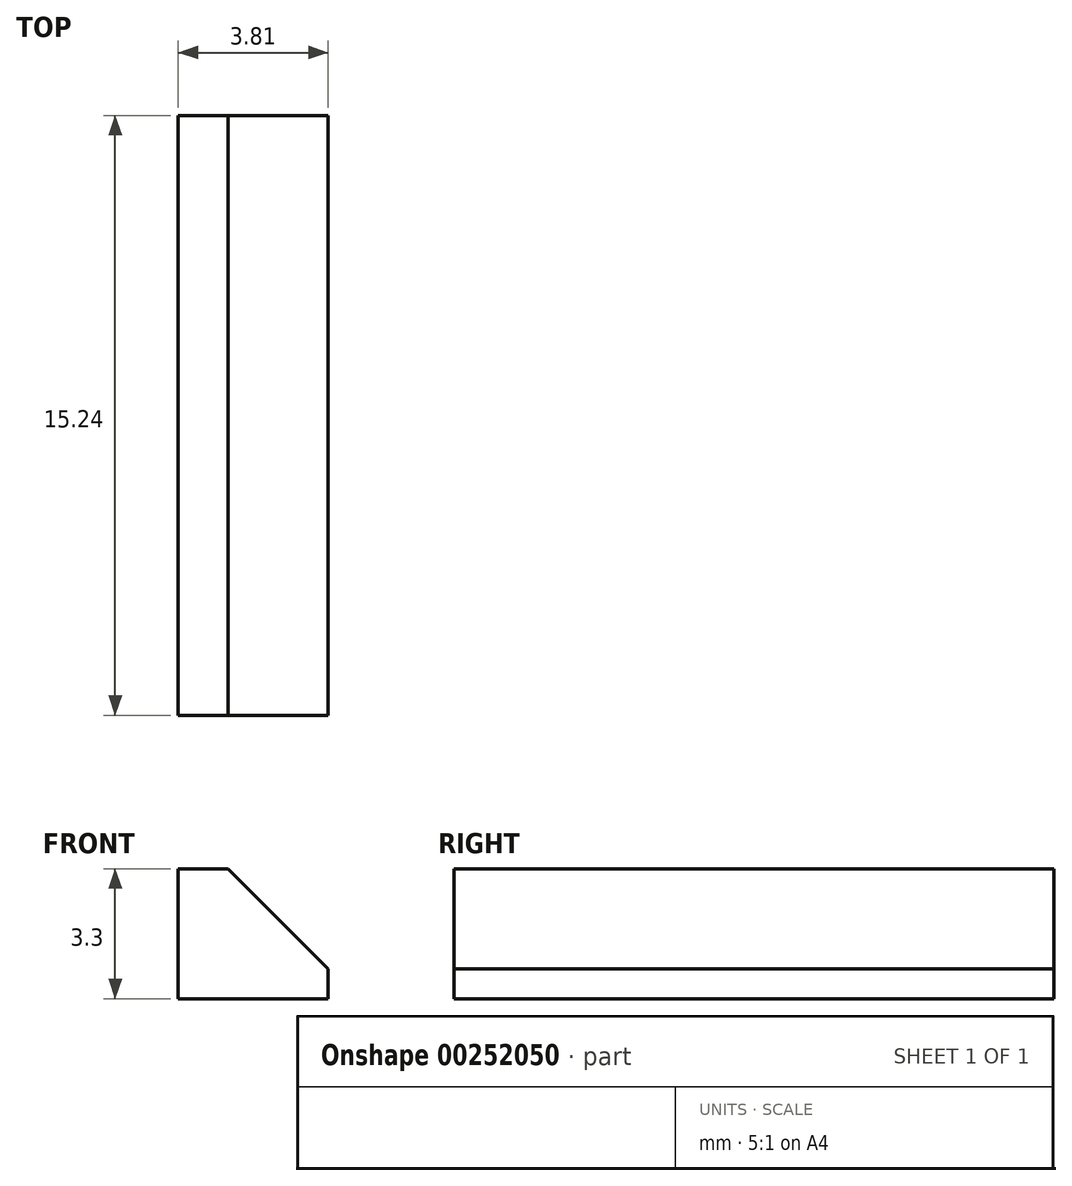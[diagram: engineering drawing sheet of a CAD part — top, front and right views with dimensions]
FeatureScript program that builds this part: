
annotation { "Feature Type Name" : "Feature", "Feature Type Description" : "" }
export const myFeature = defineFeature(function(context is Context, id is Id, definition is map)
    precondition{}
    {
        {
            var Q0;
            Q0=qCreatedBy(makeId("Right.planeOp"),FACE);
            var sketch = newSketch(context, id + "F0", { "sketchPlane" : qUnion([Q0])});
            skLineSegment(sketch, "E0.bottom", {"start": v(7.62, 1.49) * mm, "end": v(-7.62, 1.49) * mm});
            skLineSegment(sketch, "E0.top", {"start": v(7.62, -1.81) * mm, "end": v(-7.62, -1.81) * mm});
            skLineSegment(sketch, "E0.left", {"start": v(7.62, 1.49) * mm, "end": v(7.62, -1.81) * mm});
            skLineSegment(sketch, "E0.right", {"start": v(-7.62, 1.49) * mm, "end": v(-7.62, -1.81) * mm});
            skPoint(sketch, "E0.middle", {"position": v(0, -0.16) * mm});
            skSolve(sketch);
        }
        {
            var Q0;
            Q0=makeQuery(id+"F0.imprint","IMPRINT",FACE,{"disambiguationData":[TD([[makeQuery(id+"F0.imprint","IMPRINT",EDGE,{"derivedFrom":sQuery(id+"F0.wireOp",EDGE,"E0.bottom")}),1.0]])]});
            extrude(context, id + "F1", {"entities" : qUnion([Q0]), "depth" : 3.8 * mm});
        }
        {
            var Q0;
            Q0=makeQuery(id+"F1.opExtrude","CAP_EDGE",EDGE,{"disambiguationData":[OSD([sQuery(id+"F0.wireOp",EDGE,"E0.bottom")])],"isStart":false});
            chamfer(context, id + "F2", {"entities" : qUnion([Q0]), "width" : 2.54 * mm, "tangentPropagation" : true});
        }
    });
